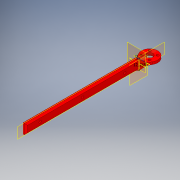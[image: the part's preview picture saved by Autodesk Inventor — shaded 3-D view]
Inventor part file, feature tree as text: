
AUTODESK INVENTOR PART (.ipt)
format: ipt  version: 2019 (Build 230136000, 136)  size: 243,200 bytes
history: native  units: mm
features: sketch x12, extrude x9, plane x8, projected_geometry x4, other x2, pattern_circular x1, mirror x1, loft x1, chamfer x1
ambient origin geometry x8: Origin, YZ Plane, XZ Plane, XY Plane, X Axis, Y Axis, Z Axis, Center Point
bodies: Solid1 (feature_tree)
feature tree (39):
  extrude  "Extrusion1"  Depth=2.0mm TaperAngle=0.0deg
  extrude  "Extrusion5"  Depth=8.0mm
  pattern_circular  "Circular Pattern2"  Count=14  [1 undecoded]
  extrude  "Extrusion6"  Depth=3.0mm TaperAngle=0.0deg
  extrude  "Extrusion7"  Depth=0.5mm TaperAngle=0.0deg
  plane  "Work Plane1"
  sketch  "Sketch8"  dims[d29=10.0mm]
  plane  "Work Plane2"
  sketch  "Sketch9"  dims[d30=5.25mm]
  plane  "Work Plane6"
  extrude  "Extrusion8"  TaperAngle=0.0deg  [1 undecoded]
  plane  "Work Plane7"
  extrude  "Extrusion9"  [1 undecoded]
  plane  "Work Plane3"
  extrude  "Extrusion10"  [1 undecoded]
  extrude  "Extrusion11"  [1 undecoded]
  plane  "Work Plane4"
  mirror  "Mirror1"
  plane  "Work Plane5"
  plane  "Work Plane8"
  extrude  "Extrusion12"  [1 undecoded]
  sketch  "Sketch17"  dims[d55=2.0mm d56=2.0mm d57=45.0deg]
  loft  "Loft2"
  chamfer  "Chamfer1"  [1 undecoded]
  sketch  "Sketch1"  dims[d2=2.0mm d3=0.0mm d19=2.0mm d20=0.0mm]
  sketch  "Sketch5"  dims[d21=40.0mm d22=360.0deg d24=8.0mm]
  sketch  "Sketch6"  dims[d25=2.0mm d26=0.0mm]
  sketch  "Sketch7"  dims[d27=1.0mm d28=0.0mm]
  projected_geometry  "Projected Loop2"
  sketch  "Sketch10"  dims[d31=3.0mm]
  projected_geometry  "Projected Loop3"
  sketch  "Sketch11"  dims[d32=12.158mm d37=140.0mm d38=0.0mm]
  sketch  "Sketch12"  dims[d40=140.0mm d41=0.0mm d43=3.0mm d44=0.0mm]
  sketch  "Sketch13"  dims[d45=3.0mm d46=0.0mm d49=0.5mm d50=0.0mm]
  sketch  "Sketch16"  dims[d51=0.0mm d52=90.0deg d53=0.0mm d54=90.0deg]
  projected_geometry  "Projected Loop6"
  projected_geometry  "Projected Loop7"
  other  "Edges1"
  other  "Edges2"
note: 7 required parameter values undecoded (feature->parameter linkage not recoverable at this tier; creation-order binding heuristic only, values carry confidence <= 0.55)
